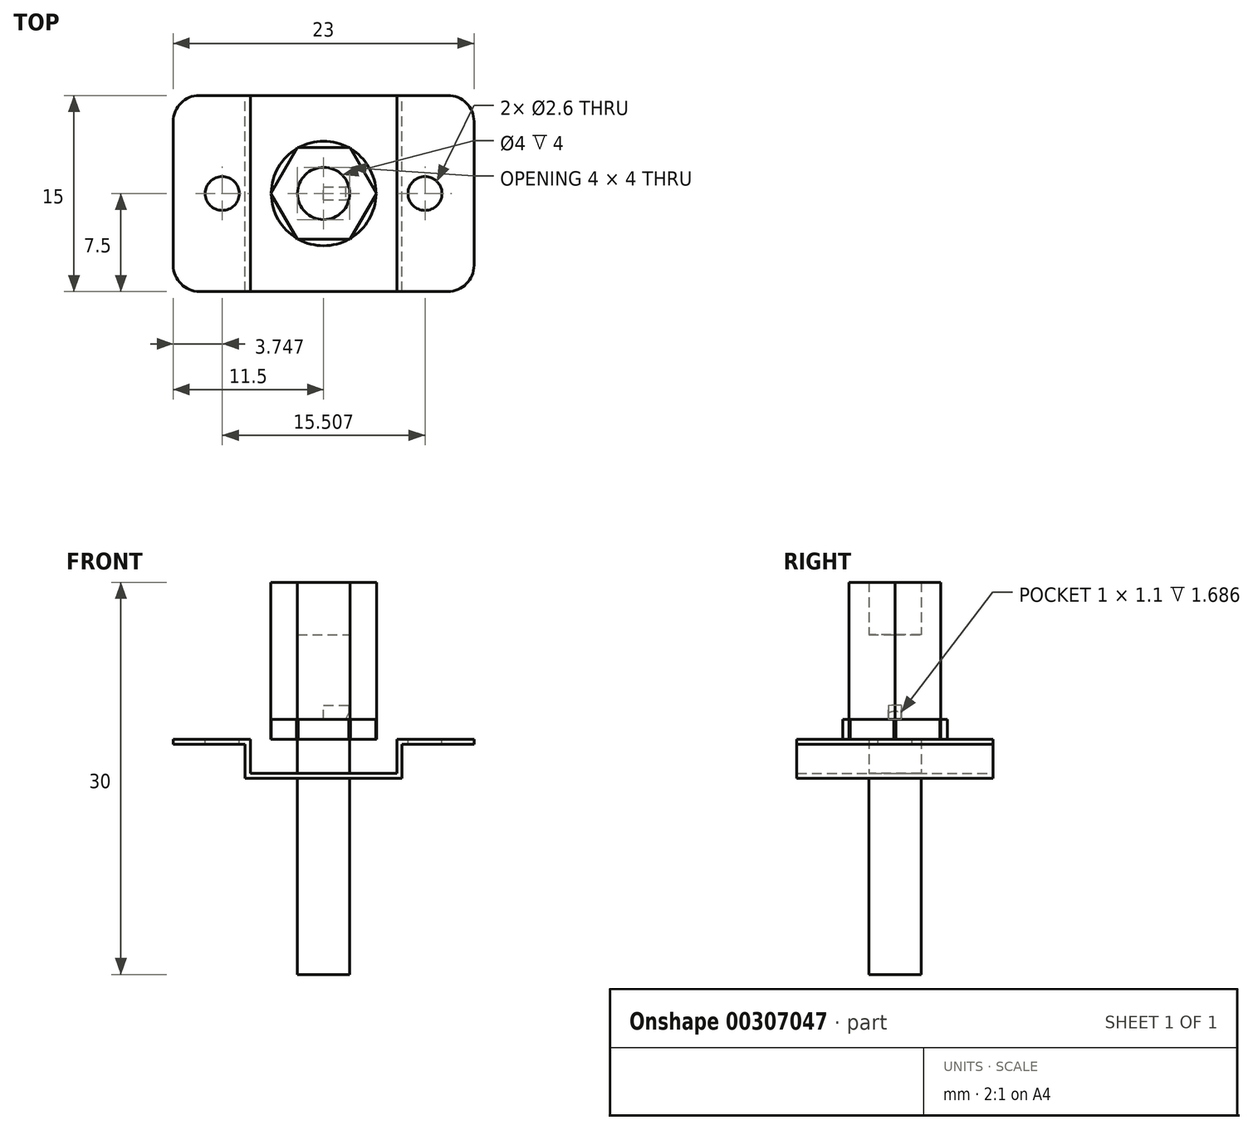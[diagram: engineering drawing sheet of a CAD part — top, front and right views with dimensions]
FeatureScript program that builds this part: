
annotation { "Feature Type Name" : "Feature", "Feature Type Description" : "" }
export const myFeature = defineFeature(function(context is Context, id is Id, definition is map)
    precondition{}
    {
        {
            var Q0;
            Q0=qCreatedBy(makeId("Front.planeOp"),FACE);
            var sketch = newSketch(context, id + "F0", { "sketchPlane" : qUnion([Q0])});
            skLineSegment(sketch, "E0", {"start": v(0, 0) * mm, "end": v(0, 8) * mm});
            skLineSegment(sketch, "E1", {"start": v(0, 8) * mm, "end": v(2.5, 8) * mm});
            skLineSegment(sketch, "E2", {"start": v(3.5, 7) * mm, "end": v(3.5, 0) * mm});
            skLineSegment(sketch, "E3", {"start": v(3.5, 0) * mm, "end": v(0, 0) * mm});
            skPoint(sketch, "E4.visualSharp", {"position": v(3.5, 8) * mm});
            skArc(sketch, "E4.filletArc", {"start": v(3.5, 7) * mm, "mid": v(3.2, 7.7) * mm, "end": v(2.5, 8) * mm});
            skSolve(sketch);
        }
        {
            var Q0;
            Q0=qSketchRegion(id+"F0",true);
            var Q1;
            Q1=sQuery(id+"F0.wireOp",EDGE,"E0");
            revolve(context, id + "F1", {"entities" : qUnion([Q0]), "axis" : qUnion([Q1]), "revolveType" : RevolveType.FULL});
        }
        {
            var Q0;
            Q0=qCreatedBy(makeId("Front.planeOp"),FACE);
            var sketch = newSketch(context, id + "F2", { "sketchPlane" : qUnion([Q0])});
            skLineSegment(sketch, "E5", {"start": v(0, 0) * mm, "end": v(3.5, 0) * mm});
            skLineSegment(sketch, "E6", {"start": v(3.5, 0) * mm, "end": v(3.5, 0.94) * mm});
            skLineSegment(sketch, "E7", {"start": v(0, 0) * mm, "end": v(0, 2.6) * mm});
            skArc(sketch, "E8", {"start": v(3.5, 0.94) * mm, "mid": v(2.96, 2.06) * mm, "end": v(1.84, 2.6) * mm});
            skLineSegment(sketch, "E9", {"start": v(0, 2.6) * mm, "end": v(1.84, 2.6) * mm});
            skSolve(sketch);
        }
        {
            var Q0;
            Q0=qSketchRegion(id+"F2",true);
            var Q1;
            Q1=sQuery(id+"F2.wireOp",EDGE,"E7");
            revolve(context, id + "F3", {"entities" : qUnion([Q0]), "axis" : qUnion([Q1]), "revolveType" : RevolveType.FULL});
        }
        {
            var Q0;
            Q0=qCreatedBy(makeId("Front.planeOp"),FACE);
            var sketch = newSketch(context, id + "F4", { "sketchPlane" : qUnion([Q0])});
            skLineSegment(sketch, "E10", {"start": v(0, 0) * mm, "end": v(2, 0) * mm});
            skLineSegment(sketch, "E11", {"start": v(2, 0) * mm, "end": v(2, -18) * mm});
            skLineSegment(sketch, "E12", {"start": v(2, -18) * mm, "end": v(0, -18) * mm});
            skLineSegment(sketch, "E13", {"start": v(0, -18) * mm, "end": v(0, 0) * mm});
            skSolve(sketch);
        }
        {
            var Q0;
            Q0=qSketchRegion(id+"F4",true);
            var Q1;
            Q1=sQuery(id+"F4.wireOp",EDGE,"E13");
            revolve(context, id + "F5", {"operationType" : NewBodyOperationType.ADD, "entities" : qUnion([Q0]), "axis" : qUnion([Q1]), "revolveType" : RevolveType.FULL});
        }
        {
            var Q0;
            Q0=qCreatedBy(makeId("Front.planeOp"),FACE);
            var sketch = newSketch(context, id + "F6", { "sketchPlane" : qUnion([Q0])});
            skLineSegment(sketch, "E14", {"start": v(0, 2.6) * mm, "end": v(2.1, 2.6) * mm});
            skLineSegment(sketch, "E15", {"start": v(2.1, 2.6) * mm, "end": v(2.1, 2.36) * mm});
            skLineSegment(sketch, "E16", {"start": v(2.1, 2.36) * mm, "end": v(1.16, 0.41) * mm});
            skLineSegment(sketch, "E17", {"start": v(1.16, 0.41) * mm, "end": v(0, 0.41) * mm});
            skLineSegment(sketch, "E18", {"start": v(0, 0.41) * mm, "end": v(0, 2.6) * mm});
            skSolve(sketch);
        }
        {
            var Q0;
            Q0=qSketchRegion(id+"F6",true);
            extrude(context, id + "F7", {"entities" : qUnion([Q0]), "operationType" : NewBodyOperationType.REMOVE, "oppositeDirection" : true, "depth" : 1 * mm, "symmetric" : true});
        }
        {
            var Q0;
            Q0=qCreatedBy(makeId("Front.planeOp"),FACE);
            var sketch = newSketch(context, id + "F8", { "sketchPlane" : qUnion([Q0])});
            skLineSegment(sketch, "E19", {"start": v(0, -3) * mm, "end": v(6, -3) * mm});
            skLineSegment(sketch, "E20", {"start": v(6, -3) * mm, "end": v(6, -0.4) * mm});
            skLineSegment(sketch, "E21", {"start": v(6, -0.4) * mm, "end": v(11.5, -0.4) * mm});
            skLineSegment(sketch, "E22", {"start": v(11.5, -0.4) * mm, "end": v(11.5, 0) * mm});
            skLineSegment(sketch, "E23", {"start": v(11.5, 0) * mm, "end": v(5.6, 0) * mm});
            skLineSegment(sketch, "E24", {"start": v(5.6, 0) * mm, "end": v(5.6, -2.6) * mm});
            skLineSegment(sketch, "E25", {"start": v(5.6, -2.6) * mm, "end": v(0, -2.6) * mm});
            skLineSegment(sketch, "E26", {"start": v(0, -2.6) * mm, "end": v(0, -3) * mm});
            skSolve(sketch);
        }
        {
            var Q0;
            Q0=qSketchRegion(id+"F8",true);
            extrude(context, id + "F9", {"entities" : qUnion([Q0]), "depth" : 15 * mm, "symmetric" : true});
        }
        {
            var Q0;
            Q0=makeQuery(id+"F9.opExtrude","SWEPT_FACE",FACE,{"disambiguationData":[OSD([sQuery(id+"F8.wireOp",EDGE,"E23")])]});
            var sketch = newSketch(context, id + "F10", { "sketchPlane" : qUnion([Q0])});
            skCircle(sketch, "E27", {"center": v(7.75, 0) * mm, "radius": 1.3 * mm});
            skSolve(sketch);
        }
        {
            var Q0;
            Q0=qSketchRegion(id+"F10",true);
            extrude(context, id + "F11", {"entities" : qUnion([Q0]), "operationType" : NewBodyOperationType.REMOVE, "oppositeDirection" : true, "depth" : 25 * mm});
        }
        {
            var Q0;
            Q0=makeQuery(id+"F9.opExtrude","CAP_EDGE",EDGE,{"disambiguationData":[OSD([sQuery(id+"F8.wireOp",EDGE,"E22")])],"isStart":true});
            var Q1;
            Q1=makeQuery(id+"F9.opExtrude","CAP_EDGE",EDGE,{"disambiguationData":[OSD([sQuery(id+"F8.wireOp",EDGE,"E22")])],"isStart":false});
            fillet(context, id + "F12", {"entities" : qUnion([Q0, Q1]), "radius" : 2 * mm, "tangentPropagation" : true, "allowEdgeOverflow" : false});
        }
        {
            var Q0;
            Q0=makeQuery(id+"F9.opExtrude","SWEPT_BODY",BODY,{"disambiguationData":[OSD([sQuery(id+"F8.wireOp",EDGE,"E19"),sQuery(id+"F8.wireOp",EDGE,"E20"),sQuery(id+"F8.wireOp",EDGE,"E21"),sQuery(id+"F8.wireOp",EDGE,"E22"),sQuery(id+"F8.wireOp",EDGE,"E23"),sQuery(id+"F8.wireOp",EDGE,"E24"),sQuery(id+"F8.wireOp",EDGE,"E25"),sQuery(id+"F8.wireOp",EDGE,"E26")])]});
            var Q1;
            Q1=makeQuery(id+"F9.opExtrude","SWEPT_FACE",FACE,{"disambiguationData":[OSD([sQuery(id+"F8.wireOp",EDGE,"E26")])]});
            mirror(context, id + "F13", {"operationType" : NewBodyOperationType.ADD, "entities" : qUnion([Q0]), "mirrorPlane" : qUnion([Q1])});
        }
        {
            var Q0;
            {var subQ0=makeQuery(id+"F9.opExtrude","SWEPT_FACE",FACE,{"disambiguationData":[OSD([sQuery(id+"F8.wireOp",EDGE,"E25")])]});Q0=makeQuery(id+"F13.boolean.opBoolean","MERGE",FACE,{"derivedFrom":[subQ0,makeQuery(id+"F13.opPattern","COPY",FACE,{"derivedFrom":subQ0,"instanceName":"1"})]});}
            var sketch = newSketch(context, id + "F14", { "sketchPlane" : qUnion([Q0])});
            skLineSegment(sketch, "E28.bottom", {"start": v(1.2, 1.2) * mm, "end": v(-1.2, 1.2) * mm});
            skLineSegment(sketch, "E28.top", {"start": v(1.2, -1.2) * mm, "end": v(-1.2, -1.2) * mm});
            skLineSegment(sketch, "E28.left", {"start": v(1.2, 1.2) * mm, "end": v(1.2, -1.2) * mm});
            skLineSegment(sketch, "E28.right", {"start": v(-1.2, 1.2) * mm, "end": v(-1.2, -1.2) * mm});
            skPoint(sketch, "E28.middle", {"position": v(0, 0) * mm});
            skSolve(sketch);
        }
        {
            var Q0;
            Q0=qSketchRegion(id+"F14",true);
            extrude(context, id + "F15", {"entities" : qUnion([Q0]), "operationType" : NewBodyOperationType.ADD, "depth" : 4 * mm});
        }
        {
            var Q0;
            Q0=qCreatedBy(makeId("Top.planeOp"),FACE);
            var sketch = newSketch(context, id + "F16", { "sketchPlane" : qUnion([Q0])});
            skCircle(sketch, "E29.cCircle", {"center": v(0, 0) * mm, "radius": 3.5 * mm, "construction": true});
            skLineSegment(sketch, "E29.0", {"start": v(-2.02, 3.5) * mm, "end": v(2.02, 3.5) * mm});
            skLineSegment(sketch, "E29.1", {"start": v(2.02, 3.5) * mm, "end": v(4.04, 0) * mm});
            skLineSegment(sketch, "E29.2", {"start": v(4.04, 0) * mm, "end": v(2.02, -3.5) * mm});
            skLineSegment(sketch, "E29.3", {"start": v(2.02, -3.5) * mm, "end": v(-2.02, -3.5) * mm});
            skLineSegment(sketch, "E29.4", {"start": v(-2.02, -3.5) * mm, "end": v(-4.04, 0) * mm});
            skLineSegment(sketch, "E29.5", {"start": v(-4.04, 0) * mm, "end": v(-2.02, 3.5) * mm});
            skPoint(sketch, "E29.0.midPoint", {"position": v(0, 3.5) * mm});
            skCircle(sketch, "E30", {"center": v(0, 0) * mm, "radius": 2 * mm});
            skSolve(sketch);
        }
        {
            var Q0;
            Q0=qSketchRegion(id+"F16",true);
            extrude(context, id + "F17", {"entities" : qUnion([Q0]), "depth" : 12 * mm});
        }
        {
            var Q0;
            Q0=qCreatedBy(makeId("Front.planeOp"),FACE);
            var sketch = newSketch(context, id + "F18", { "sketchPlane" : qUnion([Q0])});
            skLineSegment(sketch, "E31", {"start": v(0, 0) * mm, "end": v(4, 0) * mm});
            skLineSegment(sketch, "E32", {"start": v(4, 0) * mm, "end": v(4, 1.5) * mm});
            skLineSegment(sketch, "E33", {"start": v(4, 1.5) * mm, "end": v(0, 1.5) * mm});
            skLineSegment(sketch, "E34", {"start": v(0, 1.5) * mm, "end": v(0, 0) * mm});
            skSolve(sketch);
        }
        {
            var Q0;
            Q0=qSketchRegion(id+"F18",true);
            var Q1;
            Q1=sQuery(id+"F18.wireOp",EDGE,"E34");
            revolve(context, id + "F19", {"entities" : qUnion([Q0]), "axis" : qUnion([Q1]), "revolveType" : RevolveType.FULL});
        }
        {
            var Q0;
            Q0=makeQuery(id+"F19.opRevolve","SWEPT_FACE",FACE,{"disambiguationData":[OSD([sQuery(id+"F18.wireOp",EDGE,"E31")])]});
            var sketch = newSketch(context, id + "F20", { "sketchPlane" : qUnion([Q0])});
            skCircle(sketch, "E35", {"center": v(0, 0) * mm, "radius": 2 * mm});
            skSolve(sketch);
        }
        {
            var Q0;
            Q0=qSketchRegion(id+"F20",true);
            extrude(context, id + "F21", {"entities" : qUnion([Q0]), "operationType" : NewBodyOperationType.ADD, "depth" : 16 * mm});
        }
    });
